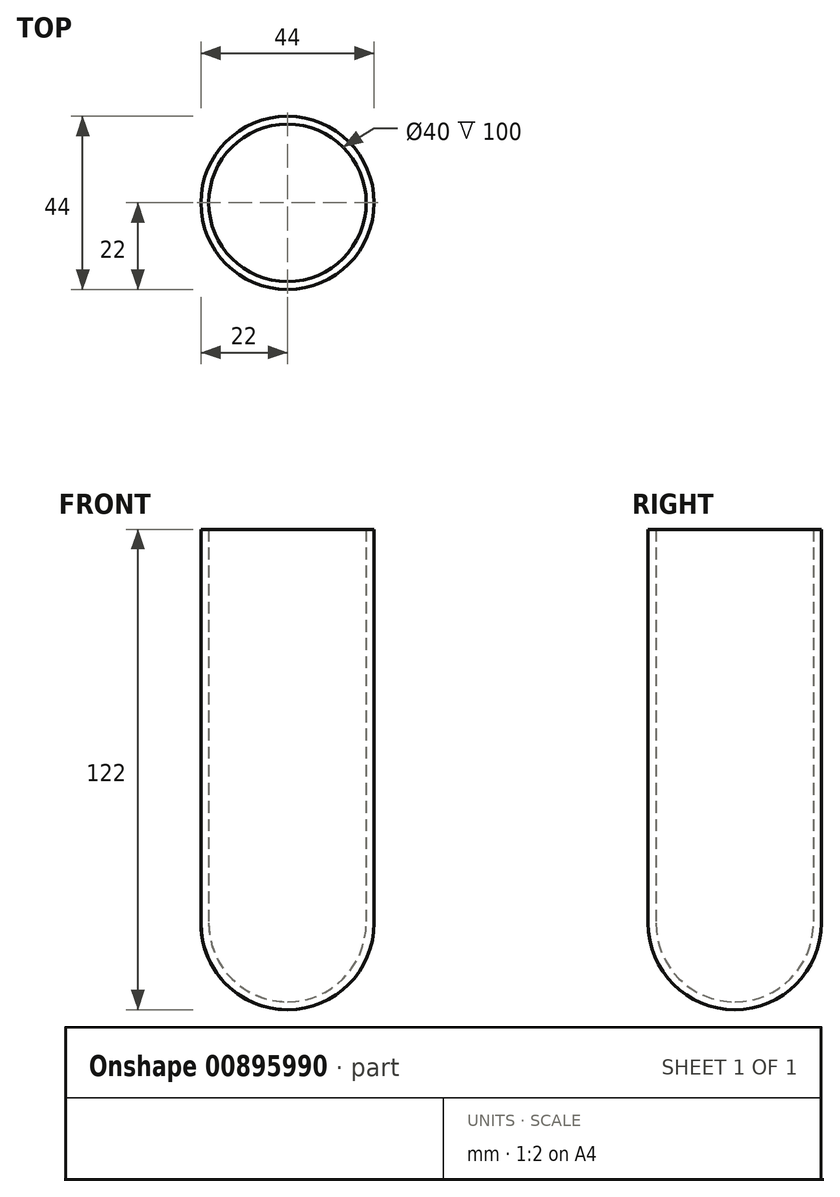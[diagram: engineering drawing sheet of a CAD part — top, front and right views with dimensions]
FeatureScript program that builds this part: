
annotation { "Feature Type Name" : "Feature", "Feature Type Description" : "" }
export const myFeature = defineFeature(function(context is Context, id is Id, definition is map)
    precondition{}
    {
        {
            var Q0;
            Q0=qCreatedBy(makeId("Front.planeOp"),FACE);
            var sketch = newSketch(context, id + "F0", { "sketchPlane" : qUnion([Q0])});
            skLineSegment(sketch, "E0", {"start": v(-20, 120) * mm, "end": v(-20, 20) * mm});
            skArc(sketch, "E1", {"start": v(-20, 20) * mm, "mid": v(-14.14, 5.86) * mm, "end": v(0, 0) * mm});
            skArc(sketch, "E2.0", {"start": v(-22, 20) * mm, "mid": v(-15.56, 4.44) * mm, "end": v(0, -2) * mm});
            skLineSegment(sketch, "E2.1", {"start": v(-22, 120) * mm, "end": v(-22, 20) * mm});
            skLineSegment(sketch, "E3", {"start": v(-22, 120) * mm, "end": v(-20, 120) * mm});
            skLineSegment(sketch, "E4", {"start": v(0, 0) * mm, "end": v(0, -2) * mm});
            skLineSegment(sketch, "E5", {"start": v(0, 0) * mm, "end": v(0, 120) * mm});
            skSolve(sketch);
        }
        {
            var Q0;
            Q0=makeQuery(id+"F0.imprint","IMPRINT",FACE,{"disambiguationData":[TD([[makeQuery(id+"F0.imprint","IMPRINT",EDGE,{"derivedFrom":sQuery(id+"F0.wireOp",EDGE,"E0")}),-1.0]])]});
            var Q1;
            Q1=sQuery(id+"F0.wireOp",EDGE,"E5");
            revolve(context, id + "F1", {"surfaceOperationType" : NewSurfaceOperationType.NEW, "entities" : qUnion([Q0]), "axis" : qUnion([Q1]), "revolveType" : RevolveType.FULL});
        }
    });
